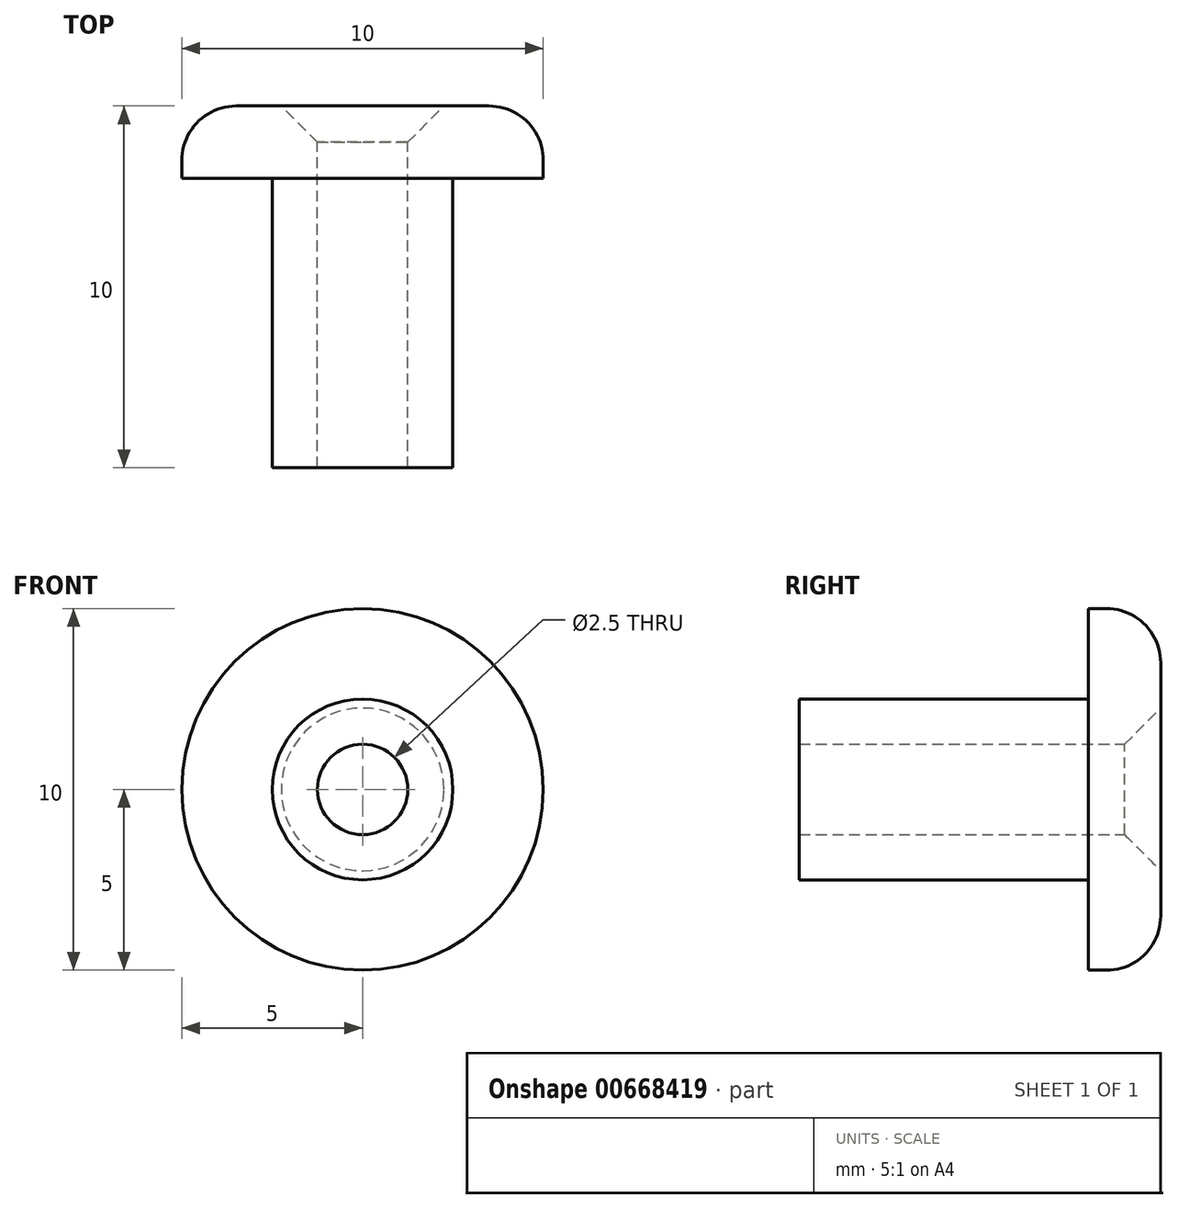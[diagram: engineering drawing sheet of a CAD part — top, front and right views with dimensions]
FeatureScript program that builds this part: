
annotation { "Feature Type Name" : "Feature", "Feature Type Description" : "" }
export const myFeature = defineFeature(function(context is Context, id is Id, definition is map)
    precondition{}
    {
        {
            var Q0;
            Q0=qCreatedBy(makeId("Front.planeOp"),FACE);
            var sketch = newSketch(context, id + "F0", { "sketchPlane" : qUnion([Q0])});
            skCircle(sketch, "E0", {"center": v(0, 0) * mm, "radius": 5 * mm});
            skCircle(sketch, "E1", {"center": v(0, 0) * mm, "radius": 2.5 * mm});
            skCircle(sketch, "E2", {"center": v(0, 0) * mm, "radius": 1.25 * mm});
            skSolve(sketch);
        }
        {
            var Q0;
            Q0=makeQuery(id+"F0.imprint","IMPRINT",FACE,{"disambiguationData":[TD([[makeQuery(id+"F0.imprint","IMPRINT",EDGE,{"derivedFrom":sQuery(id+"F0.wireOp",EDGE,"E1")}),1.0]])]});
            extrude(context, id + "F1", {"entities" : qUnion([Q0]), "depth" : 10 * mm, "offsetDistance" : 25 * mm});
        }
        {
            var Q0;
            Q0 = qSketchRegion(id + "F0", true);
            extrude(context, id + "F2", {"entities" : qUnion([Q0]), "operationType" : NewBodyOperationType.ADD, "depth" : 2 * mm, "offsetDistance" : 25 * mm});
        }
        {
            var Q0;
            Q0=makeQuery(id+"F2.opExtrude","CAP_EDGE",EDGE,{"disambiguationData":[OSD([sQuery(id+"F0.wireOp",EDGE,"E0")])],"isStart":true});
            fillet(context, id + "F3", {"entities" : qUnion([Q0]), "radius" : 1.5 * mm, "tangentPropagation" : true, "allowEdgeOverflow" : false});
        }
        {
            var Q0;
            Q0=makeQuery(id+"F1.opExtrude","CAP_EDGE",EDGE,{"disambiguationData":[OSD([sQuery(id+"F0.wireOp",EDGE,"E2")])],"isStart":true});
            chamfer(context, id + "F4", {"entities" : qUnion([Q0]), "width" : 1 * mm, "tangentPropagation" : true});
        }
    });
